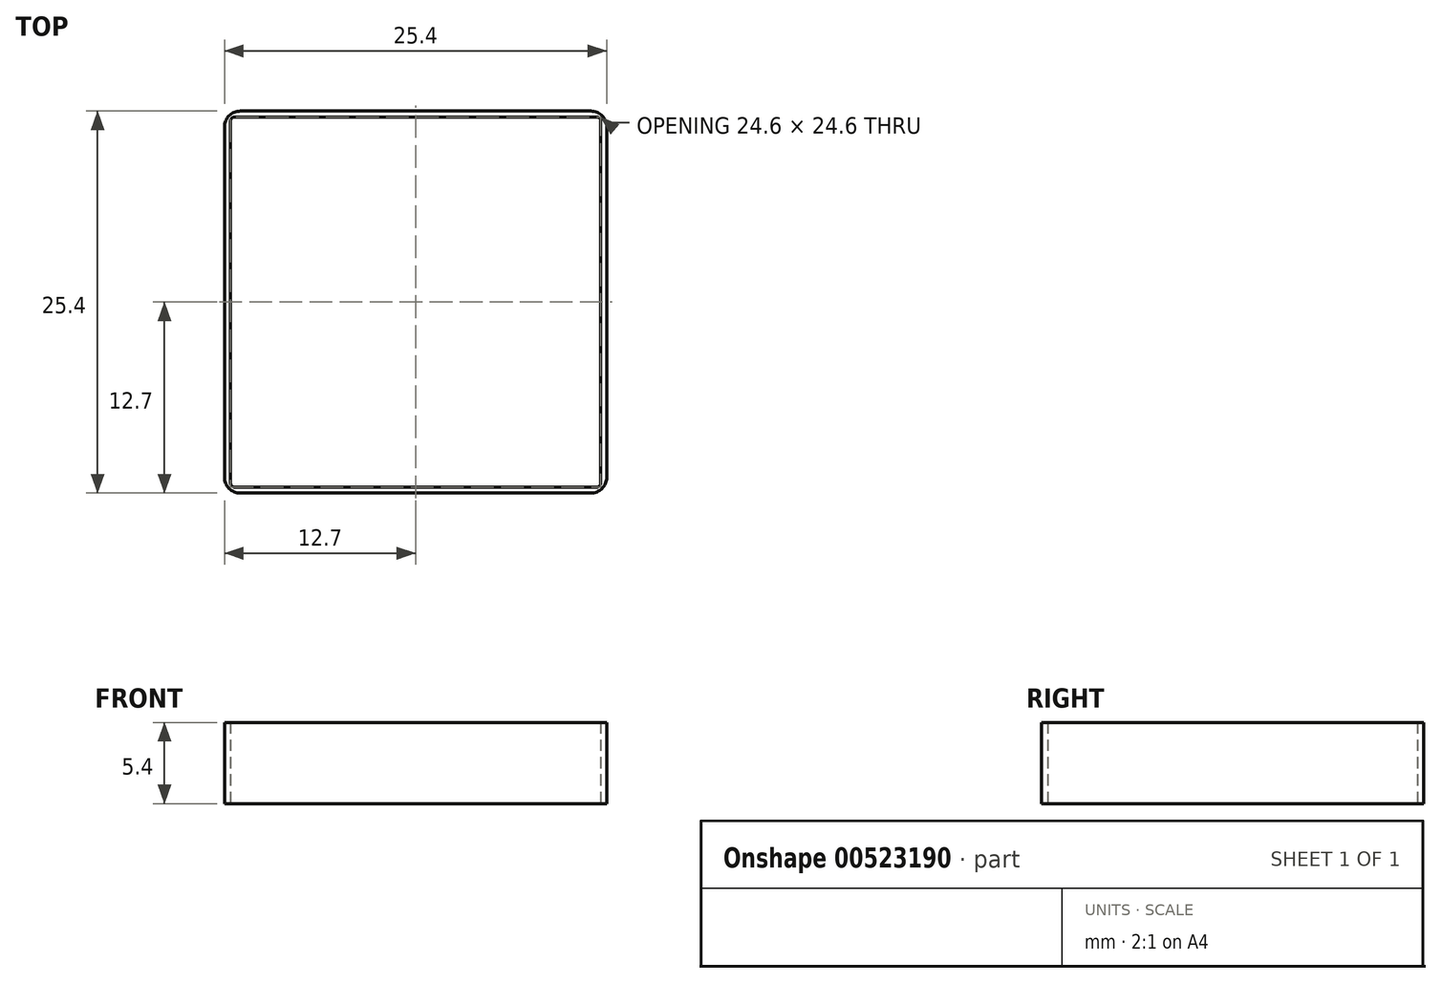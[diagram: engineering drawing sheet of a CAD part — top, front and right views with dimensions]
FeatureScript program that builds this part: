
annotation { "Feature Type Name" : "Feature", "Feature Type Description" : "" }
export const myFeature = defineFeature(function(context is Context, id is Id, definition is map)
    precondition{}
    {
        {
            var Q0;
            Q0=qCreatedBy(makeId("Top.planeOp"),FACE);
            var sketch = newSketch(context, id + "F0", { "sketchPlane" : qUnion([Q0])});
            skLineSegment(sketch, "E0.bottom", {"start": v(12.7, -12.7) * mm, "end": v(-12.7, -12.7) * mm});
            skLineSegment(sketch, "E0.top", {"start": v(12.7, 12.7) * mm, "end": v(-12.7, 12.7) * mm});
            skLineSegment(sketch, "E0.left", {"start": v(12.7, -12.7) * mm, "end": v(12.7, 12.7) * mm});
            skLineSegment(sketch, "E0.right", {"start": v(-12.7, -12.7) * mm, "end": v(-12.7, 12.7) * mm});
            skPoint(sketch, "E0.middle", {"position": v(0, 0) * mm});
            skLineSegment(sketch, "E1.0", {"start": v(-12.3, -12.3) * mm, "end": v(-12.3, 12.3) * mm});
            skLineSegment(sketch, "E1.1", {"start": v(12.3, -12.3) * mm, "end": v(-12.3, -12.3) * mm});
            skLineSegment(sketch, "E1.2", {"start": v(12.3, -12.3) * mm, "end": v(12.3, 12.3) * mm});
            skLineSegment(sketch, "E1.3", {"start": v(12.3, 12.3) * mm, "end": v(-12.3, 12.3) * mm});
            skSolve(sketch);
        }
        {
            var Q0;
            Q0=makeQuery(id+"F0.imprint","IMPRINT",FACE,{"disambiguationData":[TD([[makeQuery(id+"F0.imprint","IMPRINT",EDGE,{"derivedFrom":sQuery(id+"F0.wireOp",EDGE,"E0.bottom")}),-1.0]])]});
            extrude(context, id + "F1", {"entities" : qUnion([Q0]), "depth" : 5.4 * mm, "offsetDistance" : 25.4 * mm});
        }
        {
            var Q0;
            Q0=makeQuery(id+"F1.opExtrude","SWEPT_EDGE",EDGE,{"disambiguationData":[OSD([sQuery(id+"F0.wireOp",EDGE,"E1.2"),sQuery(id+"F0.wireOp",EDGE,"E1.3")])]});
            var Q1;
            Q1=makeQuery(id+"F1.opExtrude","SWEPT_EDGE",EDGE,{"disambiguationData":[OSD([sQuery(id+"F0.wireOp",EDGE,"E1.0"),sQuery(id+"F0.wireOp",EDGE,"E1.3")])]});
            var Q2;
            Q2=makeQuery(id+"F1.opExtrude","SWEPT_EDGE",EDGE,{"disambiguationData":[OSD([sQuery(id+"F0.wireOp",EDGE,"E1.0"),sQuery(id+"F0.wireOp",EDGE,"E1.1")])]});
            var Q3;
            Q3=makeQuery(id+"F1.opExtrude","SWEPT_EDGE",EDGE,{"disambiguationData":[OSD([sQuery(id+"F0.wireOp",EDGE,"E1.1"),sQuery(id+"F0.wireOp",EDGE,"E1.2")])]});
            fillet(context, id + "F2", {"entities" : qUnion([Q0, Q1, Q2, Q3]), "radius" : .25 * mm, "tangentPropagation" : true, "allowEdgeOverflow" : false});
        }
        {
            var Q0;
            Q0=makeQuery(id+"F1.opExtrude","SWEPT_EDGE",EDGE,{"disambiguationData":[OSD([sQuery(id+"F0.wireOp",EDGE,"E0.bottom"),sQuery(id+"F0.wireOp",EDGE,"E0.right")])]});
            var Q1;
            Q1=makeQuery(id+"F1.opExtrude","SWEPT_EDGE",EDGE,{"disambiguationData":[OSD([sQuery(id+"F0.wireOp",EDGE,"E0.top"),sQuery(id+"F0.wireOp",EDGE,"E0.right")])]});
            var Q2;
            Q2=makeQuery(id+"F1.opExtrude","SWEPT_EDGE",EDGE,{"disambiguationData":[OSD([sQuery(id+"F0.wireOp",EDGE,"E0.top"),sQuery(id+"F0.wireOp",EDGE,"E0.left")])]});
            var Q3;
            Q3=makeQuery(id+"F1.opExtrude","SWEPT_EDGE",EDGE,{"disambiguationData":[OSD([sQuery(id+"F0.wireOp",EDGE,"E0.bottom"),sQuery(id+"F0.wireOp",EDGE,"E0.left")])]});
            fillet(context, id + "F3", {"entities" : qUnion([Q0, Q1, Q2, Q3]), "radius" : (.25 + .8) * mm, "tangentPropagation" : true, "allowEdgeOverflow" : false});
        }
    });
